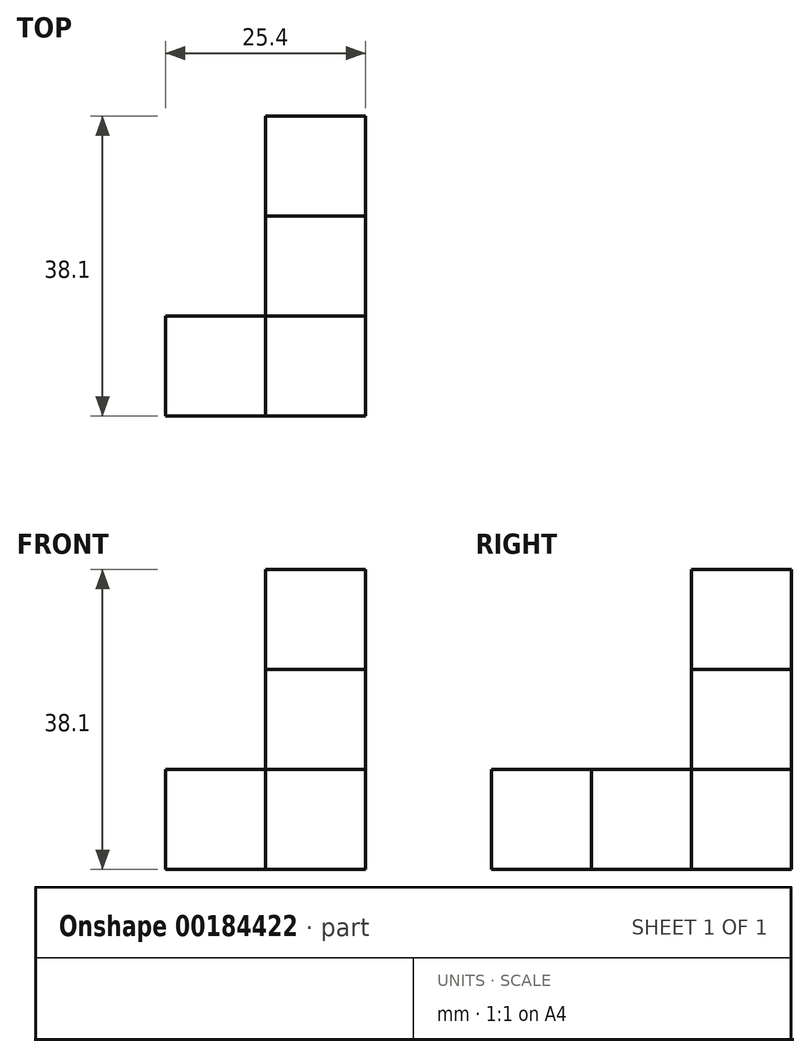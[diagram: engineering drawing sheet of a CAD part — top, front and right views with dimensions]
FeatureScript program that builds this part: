
annotation { "Feature Type Name" : "Feature", "Feature Type Description" : "" }
export const myFeature = defineFeature(function(context is Context, id is Id, definition is map)
    precondition{}
    {
        {
            var Q0;
            Q0=qCreatedBy(makeId("Front.planeOp"),FACE);
            var sketch = newSketch(context, id + "F0", { "sketchPlane" : qUnion([Q0])});
            skLineSegment(sketch, "E0", {"start": v(-32.77, -18.08) * mm, "end": v(-20.07, -18.08) * mm});
            skLineSegment(sketch, "E1", {"start": v(-20.07, -18.08) * mm, "end": v(-20.07, -5.38) * mm});
            skLineSegment(sketch, "E2", {"start": v(-20.07, -5.38) * mm, "end": v(-32.77, -5.38) * mm});
            skLineSegment(sketch, "E3", {"start": v(-32.77, -5.38) * mm, "end": v(-32.77, -18.08) * mm});
            skSolve(sketch);
        }
        {
            var Q0;
            Q0 = qSketchRegion(id + "F0", true);
            extrude(context, id + "F1", {"entities" : qUnion([Q0]), "depth" : 12.7 * mm});
        }
        {
            var Q0;
            Q0=makeQuery(id+"F1.opExtrude","SWEPT_BODY",BODY,{"disambiguationData":[OSD([sQuery(id+"F0.wireOp",EDGE,"E0"),sQuery(id+"F0.wireOp",EDGE,"E1"),sQuery(id+"F0.wireOp",EDGE,"E2"),sQuery(id+"F0.wireOp",EDGE,"E3")])]});
            var Q1;
            Q1=makeQuery(id+"F1.opExtrude","SWEPT_EDGE",EDGE,{"disambiguationData":[OSD([sQuery(id+"F0.wireOp",EDGE,"E1"),sQuery(id+"F0.wireOp",EDGE,"E2")])]});
            transform(context, id + "F2", {"entities" : qUnion([Q0]), "transformType" : TransformType.TRANSLATION_ENTITY, "oppositeDirectionEntity" : false, "transformLine" : qUnion([Q1]), "makeCopy" : true});
        }
        {
            var Q0;
            Q0=makeQuery(id+"F2.opPattern","COPY",BODY,{"derivedFrom":makeQuery(id+"F1.opExtrude","SWEPT_BODY",BODY,{"disambiguationData":[OSD([sQuery(id+"F0.wireOp",EDGE,"E0"),sQuery(id+"F0.wireOp",EDGE,"E1"),sQuery(id+"F0.wireOp",EDGE,"E2"),sQuery(id+"F0.wireOp",EDGE,"E3")])]}),"instanceName":"1"});
            var Q1;
            Q1=makeQuery(id+"F2.opPattern","COPY",EDGE,{"derivedFrom":makeQuery(id+"F1.opExtrude","SWEPT_EDGE",EDGE,{"disambiguationData":[OSD([sQuery(id+"F0.wireOp",EDGE,"E1"),sQuery(id+"F0.wireOp",EDGE,"E2")])]}),"instanceName":"1"});
            transform(context, id + "F3", {"entities" : qUnion([Q0]), "transformType" : TransformType.TRANSLATION_ENTITY, "oppositeDirectionEntity" : false, "transformLine" : qUnion([Q1]), "makeCopy" : true});
        }
        {
            var Q0;
            Q0=makeQuery(id+"F1.opExtrude","SWEPT_BODY",BODY,{"disambiguationData":[OSD([sQuery(id+"F0.wireOp",EDGE,"E0"),sQuery(id+"F0.wireOp",EDGE,"E1"),sQuery(id+"F0.wireOp",EDGE,"E2"),sQuery(id+"F0.wireOp",EDGE,"E3")])]});
            var Q1;
            Q1=makeQuery(id+"F1.opExtrude","CAP_EDGE",EDGE,{"disambiguationData":[OSD([sQuery(id+"F0.wireOp",EDGE,"E2")])],"isStart":false});
            transform(context, id + "F4", {"entities" : qUnion([Q0]), "transformType" : TransformType.TRANSLATION_ENTITY, "oppositeDirectionEntity" : false, "transformLine" : qUnion([Q1]), "makeCopy" : true});
        }
        {
            var Q0;
            Q0=makeQuery(id+"F3.opPattern","COPY",BODY,{"derivedFrom":makeQuery(id+"F2.opPattern","COPY",BODY,{"derivedFrom":makeQuery(id+"F1.opExtrude","SWEPT_BODY",BODY,{"disambiguationData":[OSD([sQuery(id+"F0.wireOp",EDGE,"E0"),sQuery(id+"F0.wireOp",EDGE,"E1"),sQuery(id+"F0.wireOp",EDGE,"E2"),sQuery(id+"F0.wireOp",EDGE,"E3")])]}),"instanceName":"1"}),"instanceName":"1"});
            transform(context, id + "F5", {"entities" : qUnion([Q0]), "transformType" : TransformType.TRANSLATION_3D, "dx" : 0 * mm, "dy" : 0 * mm, "dz" : 12.7 * mm, "makeCopy" : true});
        }
        {
            var Q0;
            Q0=makeQuery(id+"F5.opPattern","COPY",BODY,{"derivedFrom":makeQuery(id+"F3.opPattern","COPY",BODY,{"derivedFrom":makeQuery(id+"F2.opPattern","COPY",BODY,{"derivedFrom":makeQuery(id+"F1.opExtrude","SWEPT_BODY",BODY,{"disambiguationData":[OSD([sQuery(id+"F0.wireOp",EDGE,"E0"),sQuery(id+"F0.wireOp",EDGE,"E1"),sQuery(id+"F0.wireOp",EDGE,"E2"),sQuery(id+"F0.wireOp",EDGE,"E3")])]}),"instanceName":"1"}),"instanceName":"1"}),"instanceName":"1"});
            transform(context, id + "F6", {"entities" : qUnion([Q0]), "transformType" : TransformType.TRANSLATION_3D, "dx" : 0 * mm, "dy" : 0 * mm, "dz" : 12.7 * mm, "makeCopy" : true});
        }
    });
